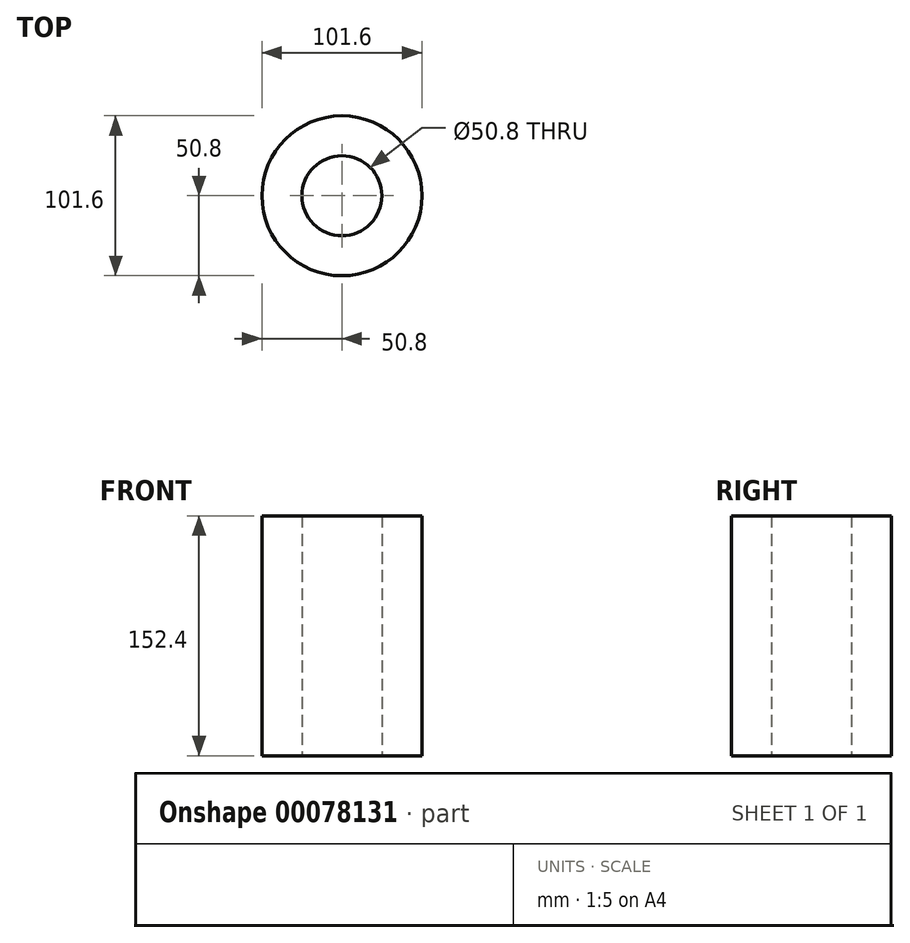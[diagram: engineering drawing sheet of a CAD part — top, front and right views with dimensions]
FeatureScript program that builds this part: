
annotation { "Feature Type Name" : "Feature", "Feature Type Description" : "" }
export const myFeature = defineFeature(function(context is Context, id is Id, definition is map)
    precondition{}
    {
        {
            var Q0;
            Q0=qCreatedBy(makeId("Top.planeOp"),FACE);
            var sketch = newSketch(context, id + "F0", { "sketchPlane" : qUnion([Q0])});
            skCircle(sketch, "E0", {"center": v(0, 0) * mm, "radius": 50.8 * mm});
            skCircle(sketch, "E1", {"center": v(0, 0) * mm, "radius": 25.4 * mm});
            skSolve(sketch);
        }
        {
            var Q0;
            Q0=makeQuery(id+"F0.imprint","IMPRINT",FACE,{"disambiguationData":[TD([[makeQuery(id+"F0.imprint","IMPRINT",EDGE,{"derivedFrom":sQuery(id+"F0.wireOp",EDGE,"E0")}),1.0]])]});
            extrude(context, id + "F1", {"entities" : qUnion([Q0]), "depth" : 152.4 * mm});
        }
    });
